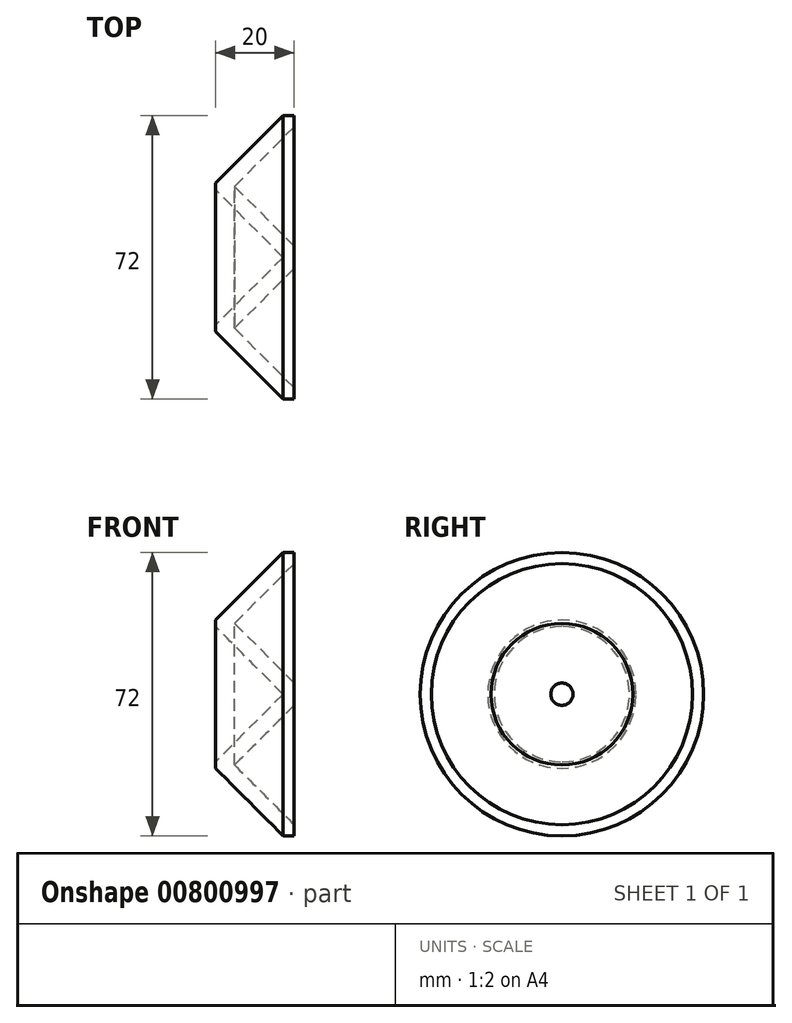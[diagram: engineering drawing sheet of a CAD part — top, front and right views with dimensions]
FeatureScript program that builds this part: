
annotation { "Feature Type Name" : "Feature", "Feature Type Description" : "" }
export const myFeature = defineFeature(function(context is Context, id is Id, definition is map)
    precondition{}
    {
        {
            var Q0;
            Q0=qCreatedBy(makeId("Top.planeOp"),FACE);
            var sketch = newSketch(context, id + "F0", { "sketchPlane" : qUnion([Q0])});
            skLineSegment(sketch, "E0", {"start": v(17.17, 0) * mm, "end": v(0, -17.17) * mm});
            skLineSegment(sketch, "E1", {"start": v(0, -17.17) * mm, "end": v(0, -18.83) * mm});
            skLineSegment(sketch, "E2", {"start": v(0, -18.83) * mm, "end": v(17.17, -36) * mm});
            skLineSegment(sketch, "E3", {"start": v(17.17, -36) * mm, "end": v(20, -36) * mm});
            skLineSegment(sketch, "E4", {"start": v(20, -36) * mm, "end": v(20, -33.17) * mm});
            skLineSegment(sketch, "E5", {"start": v(20, -33.17) * mm, "end": v(4.83, -18) * mm});
            skLineSegment(sketch, "E6", {"start": v(4.83, -18) * mm, "end": v(20, -2.83) * mm});
            skLineSegment(sketch, "E7", {"start": v(20, -2.83) * mm, "end": v(20, 0) * mm});
            skLineSegment(sketch, "E8", {"start": v(20, 0) * mm, "end": v(17.17, 0) * mm});
            skSolve(sketch);
        }
        {
            var Q0;
            Q0=makeQuery(id+"F0.imprint","IMPRINT",FACE,{"disambiguationData":[TD([[makeQuery(id+"F0.imprint","IMPRINT",EDGE,{"derivedFrom":sQuery(id+"F0.wireOp",EDGE,"E0")}),1.0]])]});
            var Q1;
            Q1=sQuery(id+"F0.wireOp",EDGE,"E8");
            revolve(context, id + "F1", {"surfaceOperationType" : NewSurfaceOperationType.NEW, "entities" : qUnion([Q0]), "axis" : qUnion([Q1]), "revolveType" : RevolveType.FULL});
        }
    });
